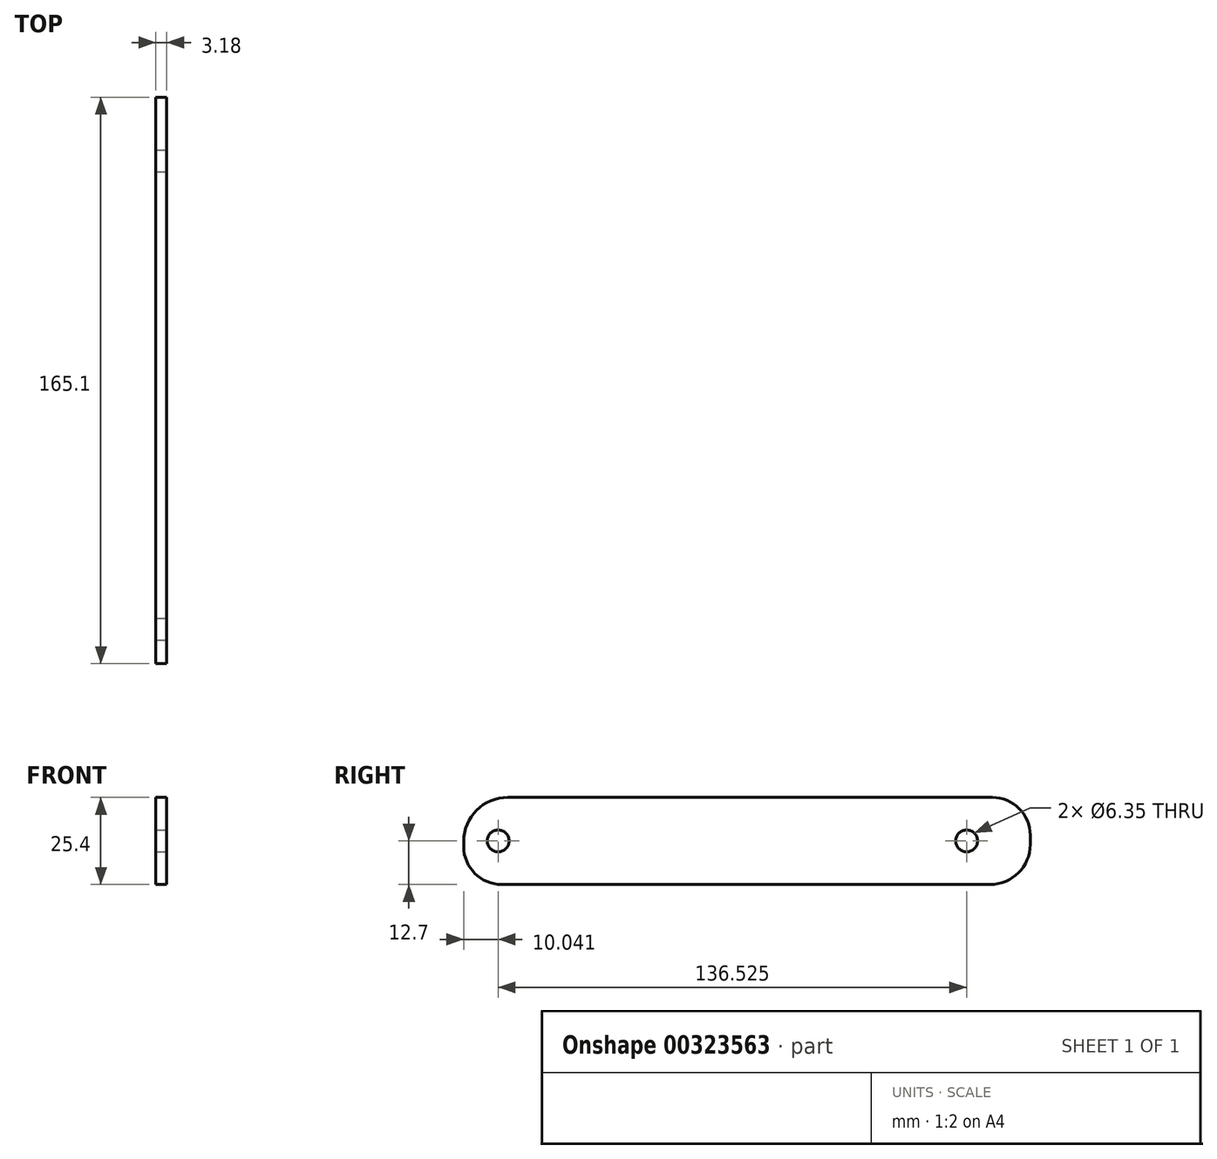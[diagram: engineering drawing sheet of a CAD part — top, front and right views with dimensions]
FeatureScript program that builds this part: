
annotation { "Feature Type Name" : "Feature", "Feature Type Description" : "" }
export const myFeature = defineFeature(function(context is Context, id is Id, definition is map)
    precondition{}
    {
        {
            var Q0;
            Q0=qCreatedBy(makeId("Right.planeOp"),FACE);
            var sketch = newSketch(context, id + "F0", { "sketchPlane" : qUnion([Q0])});
            skLineSegment(sketch, "E0.bottom", {"start": v(-82.55, 12.7) * mm, "end": v(82.55, 12.7) * mm});
            skLineSegment(sketch, "E0.top", {"start": v(-82.55, -12.7) * mm, "end": v(82.55, -12.7) * mm});
            skLineSegment(sketch, "E0.left", {"start": v(-82.55, 12.7) * mm, "end": v(-82.55, -12.7) * mm});
            skLineSegment(sketch, "E0.right", {"start": v(82.55, 12.7) * mm, "end": v(82.55, -12.7) * mm});
            skPoint(sketch, "E0.middle", {"position": v(0, 0) * mm});
            skSolve(sketch);
        }
        {
            var Q0;
            Q0=makeQuery(id+"F0.imprint","IMPRINT",FACE,{"disambiguationData":[TD([[makeQuery(id+"F0.imprint","IMPRINT",EDGE,{"derivedFrom":sQuery(id+"F0.wireOp",EDGE,"E0.bottom")}),-1.0]])]});
            extrude(context, id + "F1", {"entities" : qUnion([Q0]), "depth" : 3.17 * mm});
        }
        {
            var Q0;
            Q0=makeQuery(id+"F1.opExtrude","SWEPT_EDGE",EDGE,{"disambiguationData":[OSD([sQuery(id+"F0.wireOp",EDGE,"E0.bottom"),sQuery(id+"F0.wireOp",EDGE,"E0.left")])]});
            fillet(context, id + "F2", {"entities" : qUnion([Q0]), "radius" : 12.88 * mm, "tangentPropagation" : true, "allowEdgeOverflow" : false});
        }
        {
            var Q0;
            Q0=makeQuery(id+"F1.opExtrude","SWEPT_EDGE",EDGE,{"disambiguationData":[OSD([sQuery(id+"F0.wireOp",EDGE,"E0.top"),sQuery(id+"F0.wireOp",EDGE,"E0.left")])]});
            fillet(context, id + "F3", {"entities" : qUnion([Q0]), "radius" : 11.04 * mm, "tangentPropagation" : true, "allowEdgeOverflow" : false});
        }
        {
            var Q0;
            Q0=makeQuery(id+"F1.opExtrude","SWEPT_EDGE",EDGE,{"disambiguationData":[OSD([sQuery(id+"F0.wireOp",EDGE,"E0.bottom"),sQuery(id+"F0.wireOp",EDGE,"E0.right")])]});
            fillet(context, id + "F4", {"entities" : qUnion([Q0]), "radius" : 11.04 * mm, "tangentPropagation" : true, "allowEdgeOverflow" : false});
        }
        {
            var Q0;
            Q0=makeQuery(id+"F1.opExtrude","SWEPT_EDGE",EDGE,{"disambiguationData":[OSD([sQuery(id+"F0.wireOp",EDGE,"E0.top"),sQuery(id+"F0.wireOp",EDGE,"E0.right")])]});
            fillet(context, id + "F5", {"entities" : qUnion([Q0]), "radius" : 11.65 * mm, "tangentPropagation" : true, "allowEdgeOverflow" : false});
        }
        {
            var Q0;
            Q0=makeQuery(id+"F1.opExtrude","CAP_FACE",FACE,{"disambiguationData":[OSD([sQuery(id+"F0.wireOp",EDGE,"E0.bottom"),sQuery(id+"F0.wireOp",EDGE,"E0.top"),sQuery(id+"F0.wireOp",EDGE,"E0.left"),sQuery(id+"F0.wireOp",EDGE,"E0.right")])],"isStart":false});
            var sketch = newSketch(context, id + "F6", { "sketchPlane" : qUnion([Q0])});
            skPoint(sketch, "E1", {"position": v(-72.5, 0) * mm});
            skPoint(sketch, "E2", {"position": v(64.02, 0) * mm});
            skSolve(sketch);
        }
        {
            var Q0;
            Q0=sQuery(id+"F6.wireOp",VERTEX,"E1");
            var Q1;
            Q1=sQuery(id+"F6.wireOp",VERTEX,"E2");
            var Q2;
            Q2=makeQuery(id+"F1.opExtrude","SWEPT_BODY",BODY,{"disambiguationData":[OSD([sQuery(id+"F0.wireOp",EDGE,"E0.bottom"),sQuery(id+"F0.wireOp",EDGE,"E0.top"),sQuery(id+"F0.wireOp",EDGE,"E0.left"),sQuery(id+"F0.wireOp",EDGE,"E0.right")])]});
            hole(context, id + "F7", {"style" : HoleStyle.SIMPLE, "endStyle" : HoleEndStyle.THROUGH, "holeDiameter" : 6.35 * mm, "tappedDepth" : 12.7 * mm, "tapClearance" : 3, "locations" : qUnion([Q0, Q1]), "scope" : qUnion([Q2])});
        }
    });
